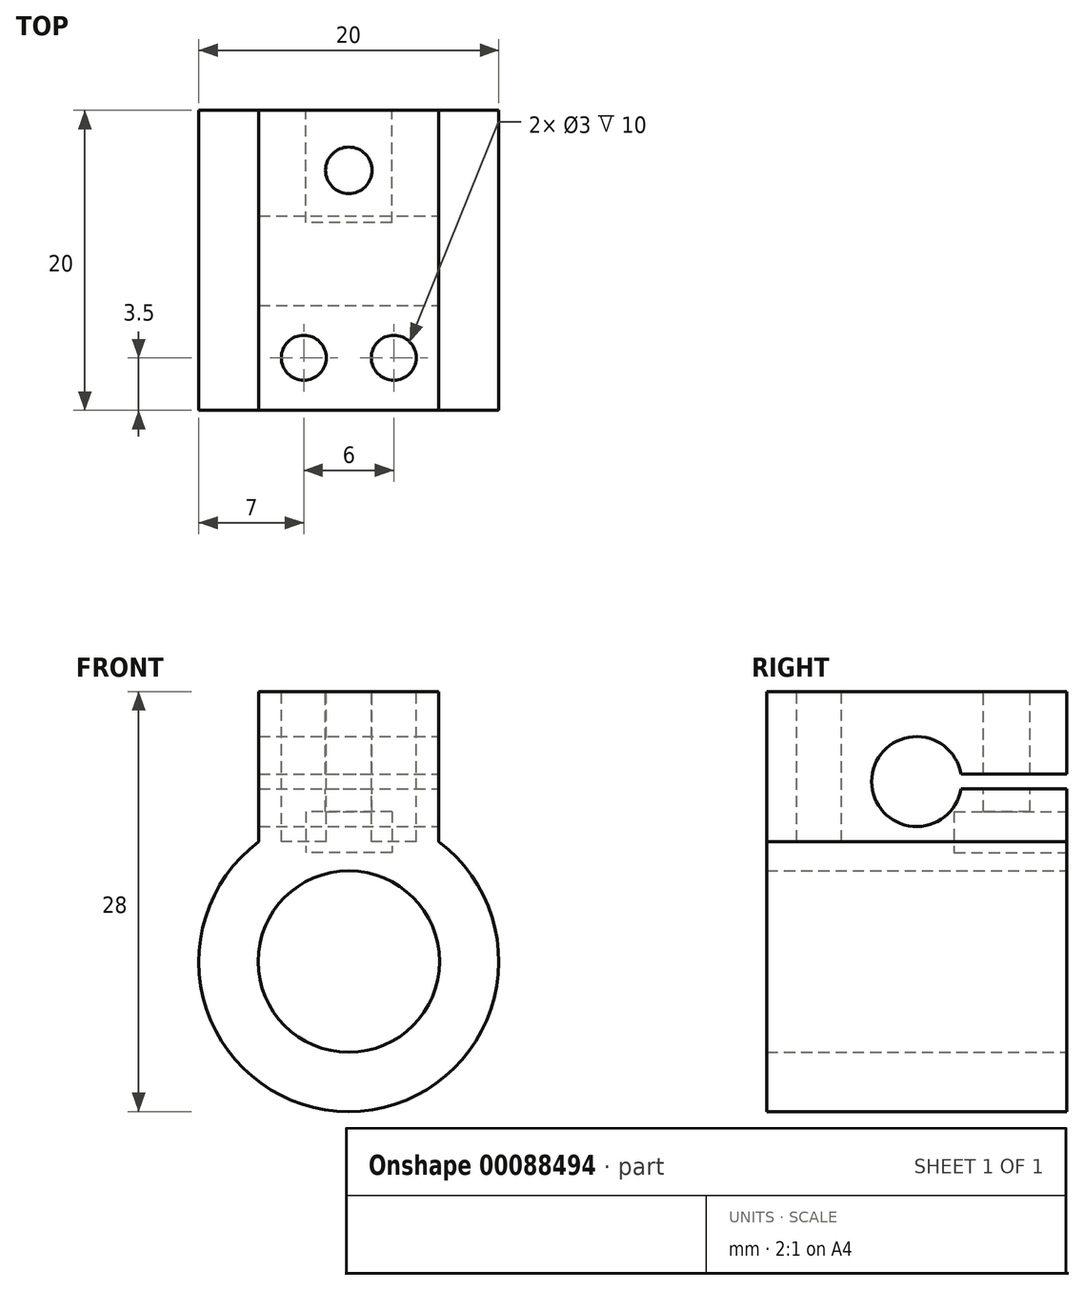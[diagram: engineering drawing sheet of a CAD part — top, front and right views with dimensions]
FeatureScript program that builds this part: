
annotation { "Feature Type Name" : "Feature", "Feature Type Description" : "" }
export const myFeature = defineFeature(function(context is Context, id is Id, definition is map)
    precondition{}
    {
        {
            var Q0;
            Q0=qCreatedBy(makeId("Front.planeOp"),FACE);
            var sketch = newSketch(context, id + "F0", { "sketchPlane" : qUnion([Q0])});
            skLineSegment(sketch, "E0", {"start": v(-6, 8) * mm, "end": v(-6, 18) * mm});
            skLineSegment(sketch, "E1", {"start": v(-6, 18) * mm, "end": v(6, 18) * mm});
            skLineSegment(sketch, "E2", {"start": v(6, 18) * mm, "end": v(6, 8) * mm});
            skCircle(sketch, "E3", {"center": v(0, 0) * mm, "radius": 6.05 * mm});
            skLineSegment(sketch, "E4", {"start": v(0, 0) * mm, "end": v(0, -10) * mm, "construction": true});
            skCircle(sketch, "E5", {"center": v(0, 12) * mm, "radius": 3 * mm, "construction": true});
            skArc(sketch, "E6.trimOffspring", {"start": v(-6, 8) * mm, "mid": v(0, -10) * mm, "end": v(6, 8) * mm});
            skSolve(sketch);
        }
        {
            var Q0;
            Q0=makeQuery(id+"F0.imprint","IMPRINT",FACE,{"disambiguationData":[TD([[makeQuery(id+"F0.imprint","IMPRINT",EDGE,{"derivedFrom":sQuery(id+"F0.wireOp",EDGE,"E0")}),-1.0]])]});
            extrude(context, id + "F1", {"entities" : qUnion([Q0]), "depth" : 20 * mm});
        }
        {
            var Q0;
            Q0=makeQuery(id+"F1.opExtrude","SWEPT_FACE",FACE,{"disambiguationData":[OSD([sQuery(id+"F0.wireOp",EDGE,"E2")])]});
            var sketch = newSketch(context, id + "F2", { "sketchPlane" : qUnion([Q0])});
            skArc(sketch, "E7", {"start": v(-7.04, 12.5) * mm, "mid": v(-13, 12) * mm, "end": v(-7.04, 11.5) * mm});
            skLineSegment(sketch, "E8", {"start": v(-7.04, 12.5) * mm, "end": v(0, 12.5) * mm});
            skLineSegment(sketch, "E9", {"start": v(-7.04, 11.5) * mm, "end": v(0, 11.5) * mm});
            skLineSegment(sketch, "E10", {"start": v(0, 12.5) * mm, "end": v(0, 11.5) * mm});
            skSolve(sketch);
        }
        {
            var Q0;
            Q0 = qSketchRegion(id + "F2", true);
            extrude(context, id + "F3", {"entities" : qUnion([Q0]), "operationType" : NewBodyOperationType.REMOVE, "oppositeDirection" : true, "depth" : 25 * mm});
        }
        {
            var Q0;
            {var subQ0=sQuery(id+"F0.wireOp",EDGE,"E6.trimOffspring");var subQ1=sQuery(id+"F0.wireOp",EDGE,"E3");var subQ2=sQuery(id+"F0.wireOp",EDGE,"E2");var subQ3=sQuery(id+"F0.wireOp",EDGE,"E0");Q0=makeQuery(id+"F3.boolean.opBoolean","SPLIT",FACE,{"disambiguationData":[TD([makeQuery(id+"F1.opExtrude","SWEPT_FACE",FACE,{"disambiguationData":[OSD([subQ1])]})])],"derivedFrom":makeQuery(id+"F1.opExtrude","CAP_FACE",FACE,{"disambiguationData":[OSD([subQ3,sQuery(id+"F0.wireOp",EDGE,"E1"),subQ2,subQ1,subQ0,sQuery(id+"F0.wireOp",EDGE,"c32d9758-957b-4987-aa54-74a0080b717f.filletArc"),sQuery(id+"F0.wireOp",EDGE,"a0691a14-58ba-40bc-be37-97391b088e77.filletArc")])],"isStart":true})});}
            var sketch = newSketch(context, id + "F4", { "sketchPlane" : qUnion([Q0])});
            skLineSegment(sketch, "E11.bottom", {"start": v(-2.88, 10) * mm, "end": v(2.87, 10) * mm});
            skLineSegment(sketch, "E11.top", {"start": v(-2.88, 7.25) * mm, "end": v(2.87, 7.25) * mm});
            skLineSegment(sketch, "E11.left", {"start": v(-2.88, 10) * mm, "end": v(-2.88, 7.25) * mm});
            skLineSegment(sketch, "E11.right", {"start": v(2.87, 10) * mm, "end": v(2.87, 7.25) * mm});
            skPoint(sketch, "E12", {"position": v(0, 7.25) * mm});
            skSolve(sketch);
        }
        {
            var Q0;
            Q0 = qSketchRegion(id + "F4", true);
            extrude(context, id + "F5", {"entities" : qUnion([Q0]), "operationType" : NewBodyOperationType.REMOVE, "oppositeDirection" : true, "depth" : 7.5 * mm});
        }
        {
            var Q0;
            Q0=makeQuery(id+"F1.opExtrude","SWEPT_FACE",FACE,{"disambiguationData":[OSD([sQuery(id+"F0.wireOp",EDGE,"E1")])]});
            var sketch = newSketch(context, id + "F6", { "sketchPlane" : qUnion([Q0])});
            skCircle(sketch, "E13", {"center": v(0, -4) * mm, "radius": 1.55 * mm});
            skPoint(sketch, "E13.centerSnap0", {"position": v(0, -20) * mm});
            skSolve(sketch);
        }
        {
            var Q0;
            Q0 = qSketchRegion(id + "F6", true);
            extrude(context, id + "F7", {"entities" : qUnion([Q0]), "operationType" : NewBodyOperationType.REMOVE, "oppositeDirection" : true, "depth" : 10 * mm});
        }
        {
            var Q0;
            Q0=makeQuery(id+"F1.opExtrude","SWEPT_FACE",FACE,{"disambiguationData":[OSD([sQuery(id+"F0.wireOp",EDGE,"E1")])]});
            var sketch = newSketch(context, id + "F8", { "sketchPlane" : qUnion([Q0])});
            skCircle(sketch, "E14.cCircle", {"center": v(0, -4) * mm, "radius": 2.75 * mm, "construction": true});
            skLineSegment(sketch, "E14.0", {"start": v(0, -7.18) * mm, "end": v(-2.75, -5.59) * mm});
            skLineSegment(sketch, "E14.1", {"start": v(-2.75, -5.59) * mm, "end": v(-2.75, -2.41) * mm});
            skLineSegment(sketch, "E14.2", {"start": v(-2.75, -2.41) * mm, "end": v(0, -0.82) * mm});
            skLineSegment(sketch, "E14.3", {"start": v(0, -0.82) * mm, "end": v(2.75, -2.41) * mm});
            skLineSegment(sketch, "E14.4", {"start": v(2.75, -2.41) * mm, "end": v(2.75, -5.59) * mm});
            skLineSegment(sketch, "E14.5", {"start": v(2.75, -5.59) * mm, "end": v(0, -7.18) * mm});
            skPoint(sketch, "E14.0.midPoint", {"position": v(-1.37, -6.38) * mm});
            skSolve(sketch);
        }
        {
            var Q0;
            Q0=makeQuery(id+"F8.imprint","IMPRINT",FACE,{"disambiguationData":[TD([[makeQuery(id+"F8.imprint","IMPRINT",EDGE,{"derivedFrom":sQuery(id+"F8.wireOp",EDGE,"E14.0")}),1.0]])]});
            var sketch = newSketch(context, id + "F9", { "sketchPlane" : qUnion([Q0])});
            skCircle(sketch, "E15", {"center": v(-3, -16.5) * mm, "radius": 1.5 * mm});
            skCircle(sketch, "E16", {"center": v(3, -16.5) * mm, "radius": 1.5 * mm});
            skLineSegment(sketch, "E17", {"start": v(3, -16.5) * mm, "end": v(0, -16.5) * mm, "construction": true});
            skLineSegment(sketch, "E18", {"start": v(0, -16.5) * mm, "end": v(-3, -16.5) * mm, "construction": true});
            skSolve(sketch);
        }
        {
            var Q0;
            Q0 = qSketchRegion(id + "F9", true);
            extrude(context, id + "F10", {"entities" : qUnion([Q0]), "operationType" : NewBodyOperationType.REMOVE, "oppositeDirection" : true, "depth" : 10 * mm});
        }
    });
